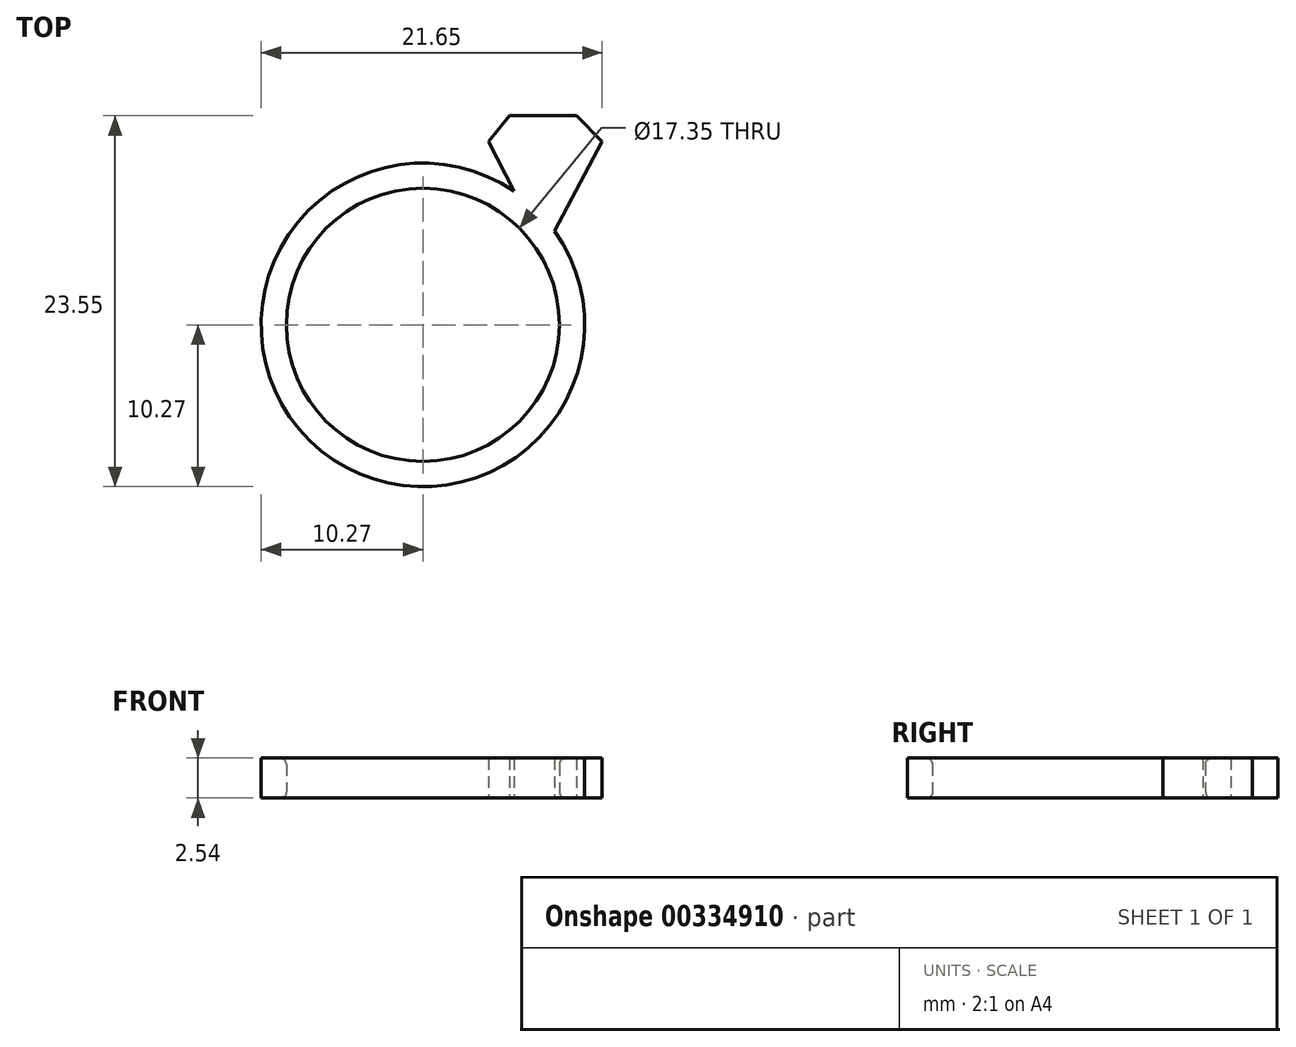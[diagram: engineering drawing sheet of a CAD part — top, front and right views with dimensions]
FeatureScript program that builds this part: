
annotation { "Feature Type Name" : "Feature", "Feature Type Description" : "" }
export const myFeature = defineFeature(function(context is Context, id is Id, definition is map)
    precondition{}
    {
        {
            var Q0;
            Q0=qCreatedBy(makeId("Top.planeOp"),FACE);
            var sketch = newSketch(context, id + "F0", { "sketchPlane" : qUnion([Q0])});
            skCircle(sketch, "E0", {"center": v(0, 0) * mm, "radius": 8.67 * mm});
            skArc(sketch, "E1.0", {"start": v(5.8, 8.48) * mm, "mid": v(-7.19, -7.34) * mm, "end": v(8.36, 5.97) * mm});
            skLineSegment(sketch, "E2", {"start": v(4.17, 11.64) * mm, "end": v(5.52, 13.28) * mm});
            skLineSegment(sketch, "E3", {"start": v(5.52, 13.28) * mm, "end": v(9.75, 13.28) * mm});
            skLineSegment(sketch, "E4", {"start": v(9.75, 13.28) * mm, "end": v(11.38, 11.64) * mm});
            skPoint(sketch, "E5.end.orphan", {"position": v(6.29, 9.42) * mm});
            skPoint(sketch, "E5.start.orphan", {"position": v(6.2, 11.34) * mm});
            skLineSegment(sketch, "E6", {"start": v(4.17, 11.64) * mm, "end": v(5.8, 8.48) * mm});
            skLineSegment(sketch, "E7", {"start": v(11.38, 11.64) * mm, "end": v(8.36, 5.97) * mm});
            skPoint(sketch, "E8.orphan", {"position": v(7.83, 7.5) * mm});
            skSolve(sketch);
        }
        {
            var Q0;
            Q0 = qSketchRegion(id + "F0", true);
            extrude(context, id + "F1", {"entities" : qUnion([Q0]), "depth" : 2.54 * mm});
        }
        {
            var Q0;
            Q0=makeQuery(id+"F1.opExtrude","CAP_EDGE",EDGE,{"disambiguationData":[OSD([sQuery(id+"F0.wireOp",EDGE,"E0")])],"isStart":true});
            var Q1;
            Q1=makeQuery(id+"F1.opExtrude","CAP_EDGE",EDGE,{"disambiguationData":[OSD([sQuery(id+"F0.wireOp",EDGE,"E0")])],"isStart":false});
            fillet(context, id + "F2", {"entities" : qUnion([Q0, Q1]), "radius" : 0.38 * mm, "tangentPropagation" : true, "allowEdgeOverflow" : false});
        }
    });
